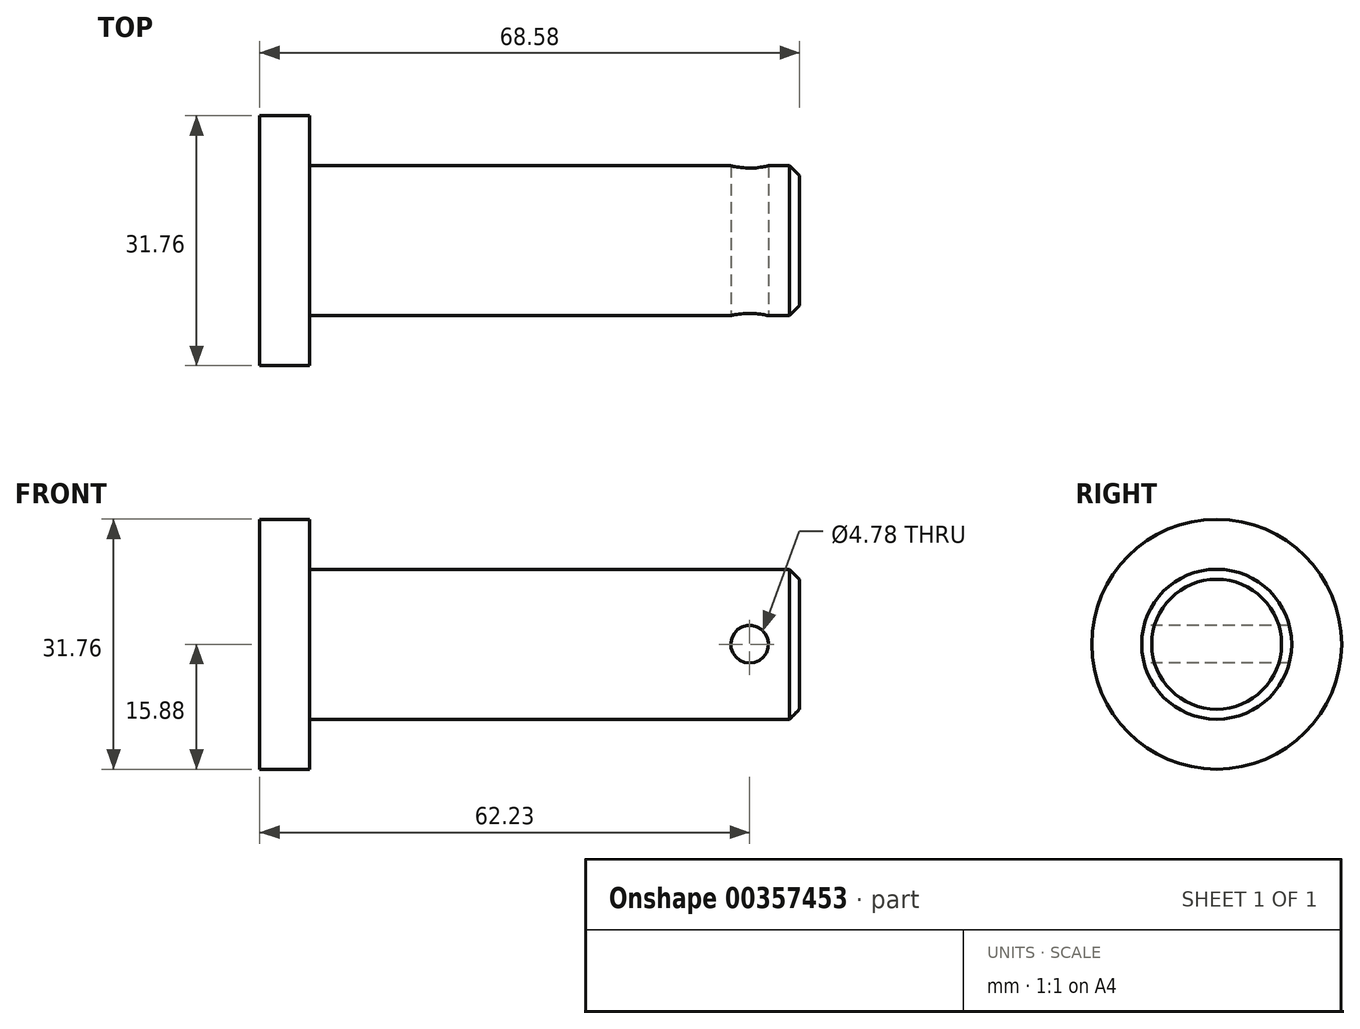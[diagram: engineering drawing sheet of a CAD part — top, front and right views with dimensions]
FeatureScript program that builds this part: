
annotation { "Feature Type Name" : "Feature", "Feature Type Description" : "" }
export const myFeature = defineFeature(function(context is Context, id is Id, definition is map)
    precondition{}
    {
        {
            var Q0;
            Q0=qCreatedBy(makeId("Right.planeOp"),FACE);
            var sketch = newSketch(context, id + "F0", { "sketchPlane" : qUnion([Q0])});
            skCircle(sketch, "E0", {"center": v(0, 0) * mm, "radius": 9.53 * mm});
            skSolve(sketch);
        }
        {
            var Q0;
            Q0 = qSketchRegion(id + "F0", true);
            extrude(context, id + "F1", {"entities" : qUnion([Q0]), "depth" : 62.23 * mm});
        }
        {
            var Q0;
            Q0=qCreatedBy(makeId("Front.planeOp"),FACE);
            var sketch = newSketch(context, id + "F2", { "sketchPlane" : qUnion([Q0])});
            skCircle(sketch, "E1", {"center": v(55.88, 0) * mm, "radius": 2.39 * mm});
            skSolve(sketch);
        }
        {
            var Q0;
            Q0 = qSketchRegion(id + "F2", true);
            extrude(context, id + "F3", {"entities" : qUnion([Q0]), "operationType" : NewBodyOperationType.REMOVE, "endBound" : BoundingType.THROUGH_ALL, "oppositeDirection" : true, "depth" : 25.4 * mm, "hasSecondDirection" : true, "secondDirectionBound" : SecondDirectionBoundingType.THROUGH_ALL, "secondDirectionOppositeDirection" : false, "secondDirectionDepth" : 25.4 * mm});
        }
        {
            var Q0;
            Q0=qCreatedBy(makeId("Right.planeOp"),FACE);
            var sketch = newSketch(context, id + "F4", { "sketchPlane" : qUnion([Q0])});
            skCircle(sketch, "E2", {"center": v(0, 0) * mm, "radius": 15.88 * mm});
            skSolve(sketch);
        }
        {
            var Q0;
            Q0 = qSketchRegion(id + "F4", true);
            extrude(context, id + "F5", {"entities" : qUnion([Q0]), "operationType" : NewBodyOperationType.ADD, "oppositeDirection" : true, "depth" : 6.35 * mm});
        }
        {
            var Q0;
            Q0=makeQuery(id+"F1.opExtrude","CAP_EDGE",EDGE,{"disambiguationData":[OSD([sQuery(id+"F0.wireOp",EDGE,"E0")])],"isStart":false});
            chamfer(context, id + "F6", {"entities" : qUnion([Q0]), "chamferType" : ChamferType.OFFSET_ANGLE, "width" : 1.27 * mm, "oppositeDirection" : false, "angle" : 45 * degree, "tangentPropagation" : true});
        }
    });
